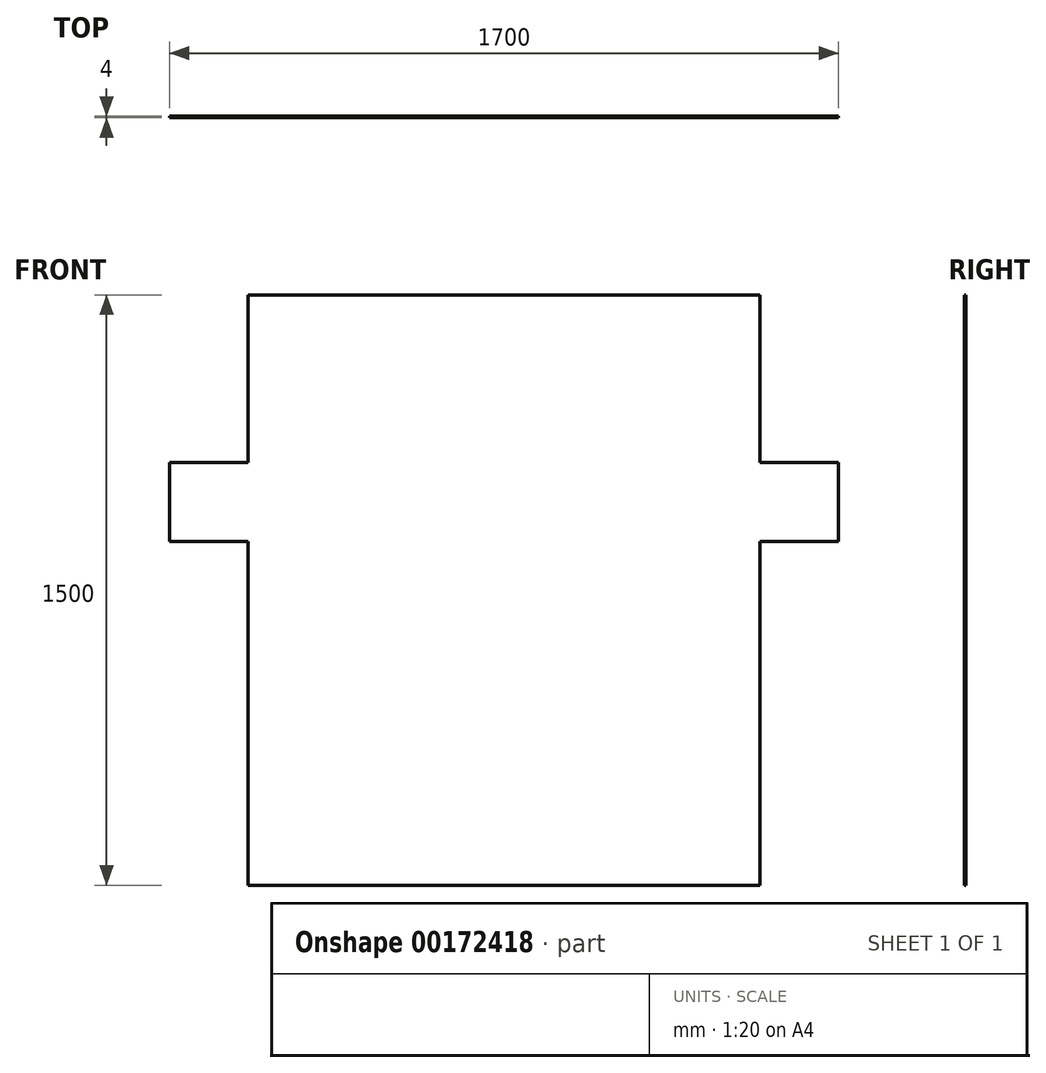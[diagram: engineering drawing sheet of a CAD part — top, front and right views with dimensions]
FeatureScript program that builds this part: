
annotation { "Feature Type Name" : "Feature", "Feature Type Description" : "" }
export const myFeature = defineFeature(function(context is Context, id is Id, definition is map)
    precondition{}
    {
        {
            var Q0;
            Q0=qCreatedBy(makeId("Front.planeOp"),FACE);
            var sketch = newSketch(context, id + "F0", { "sketchPlane" : qUnion([Q0])});
            skLineSegment(sketch, "E0", {"start": v(649.3, 638.9) * mm, "end": v(649.3, 438.9) * mm});
            skLineSegment(sketch, "E1", {"start": v(649.3, 438.9) * mm, "end": v(449.3, 438.9) * mm});
            skLineSegment(sketch, "E2", {"start": v(449.3, 438.9) * mm, "end": v(449.3, -435.1) * mm});
            skLineSegment(sketch, "E3", {"start": v(449.3, -435.1) * mm, "end": v(-850.7, -435.1) * mm});
            skLineSegment(sketch, "E4", {"start": v(-850.7, -435.1) * mm, "end": v(-850.7, 438.9) * mm});
            skLineSegment(sketch, "E5", {"start": v(-850.7, 438.9) * mm, "end": v(-1050.7, 438.9) * mm});
            skLineSegment(sketch, "E6", {"start": v(-1050.7, 438.9) * mm, "end": v(-1050.7, 638.9) * mm});
            skLineSegment(sketch, "E7", {"start": v(-1050.7, 638.9) * mm, "end": v(-850.7, 638.9) * mm});
            skLineSegment(sketch, "E8", {"start": v(-850.7, 638.9) * mm, "end": v(-850.7, 1064.9) * mm});
            skLineSegment(sketch, "E9", {"start": v(-850.7, 1064.9) * mm, "end": v(449.3, 1064.9) * mm});
            skLineSegment(sketch, "E10", {"start": v(449.3, 1064.9) * mm, "end": v(449.3, 638.9) * mm});
            skLineSegment(sketch, "E11", {"start": v(449.3, 638.9) * mm, "end": v(649.3, 638.9) * mm});
            skSolve(sketch);
        }
        {
            var Q0;
            Q0=makeQuery(id+"F0.imprint","IMPRINT",FACE,{"disambiguationData":[TD([[makeQuery(id+"F0.imprint","IMPRINT",EDGE,{"derivedFrom":sQuery(id+"F0.wireOp",EDGE,"aWVP8CCG-WWuF-vRwY-zIit-YdMqIcWi3kGc")}),-1.0]])]});
            var Q1;
            Q1=makeQuery(id+"F0.imprint","IMPRINT",FACE,{"disambiguationData":[TD([[makeQuery(id+"F0.imprint","IMPRINT",EDGE,{"derivedFrom":sQuery(id+"F0.wireOp",EDGE,"E0")}),-1.0]])]});
            extrude(context, id + "F1", {"entities" : qUnion([Q0, Q1]), "depth" : 4 * mm});
        }
    });
